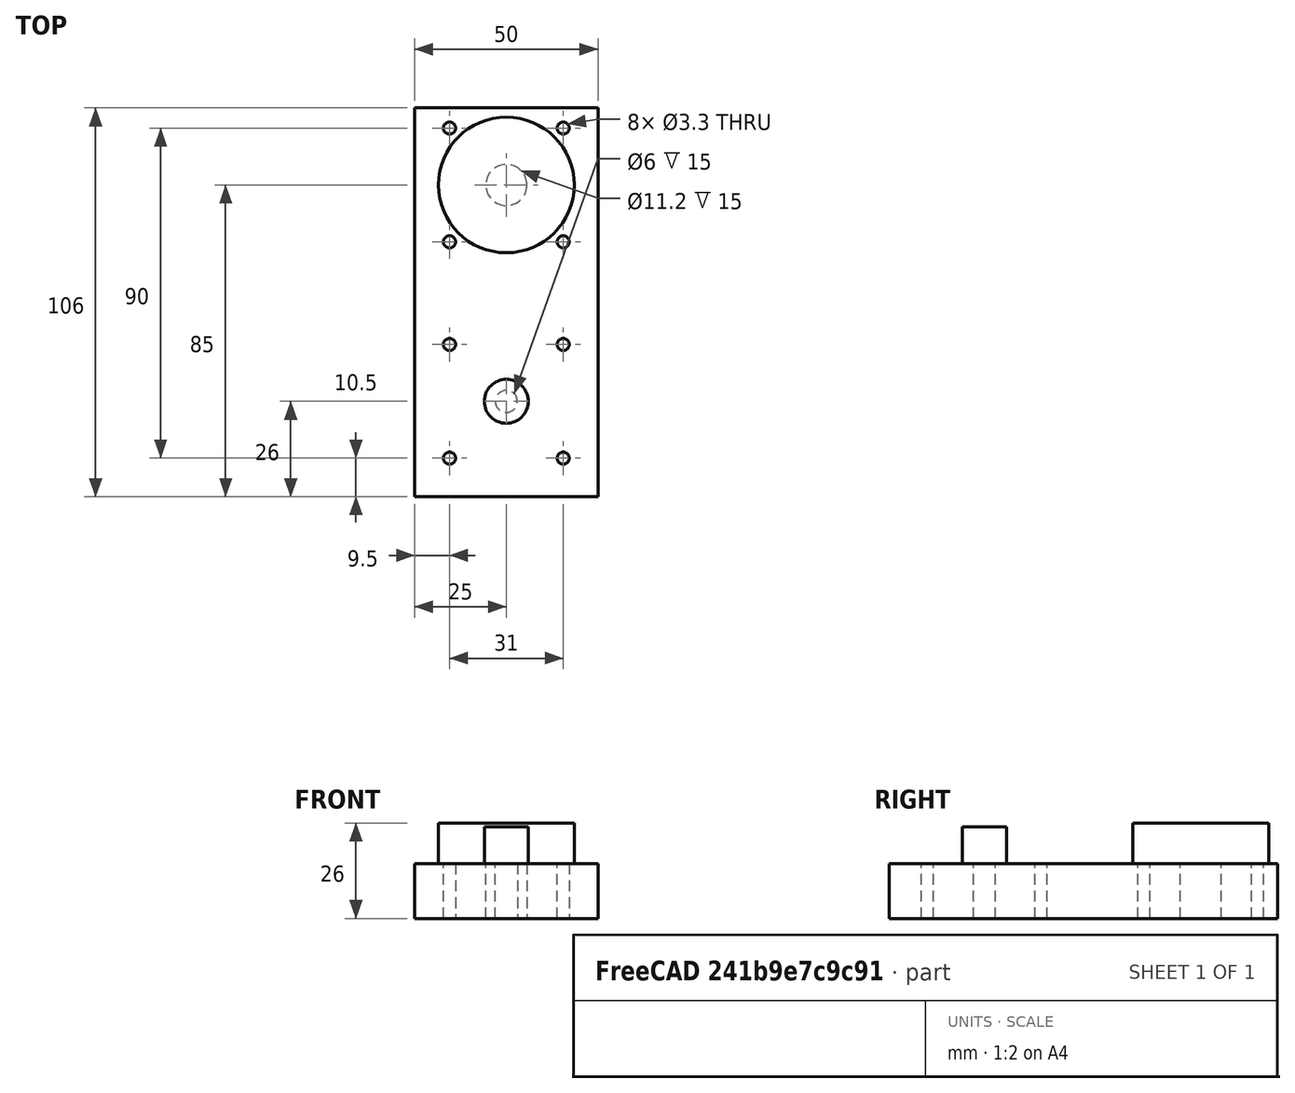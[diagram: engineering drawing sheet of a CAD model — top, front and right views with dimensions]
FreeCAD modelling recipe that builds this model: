
FCSTD DOCUMENT  (FreeCAD 0.19R)
Label: ConsBelt
License: All rights reserved
LicenseURL: http://en.wikipedia.org/wiki/All_rights_reserved
objects: Sketcher::SketchObject×5, PartDesign::Pad×3, PartDesign::Pocket×2, PartDesign::Body×1, Mesh::Feature×1
note: 16 computed .brp shape members not serialized (recipe doc carries the construction recipe); baked Part::Feature solids carry a one-line shape summary decoded from their .brp

FEATURE [Sketcher::SketchObject] Sketch
  FullyConstrained = true
  MapMode = 5
  Support = -> [XY_Plane]
  sketch-geometry (9):
    g0: Circle CenterX=0 CenterY=0 CenterZ=0 NormalX=0 NormalY=0 NormalZ=1 AngleXU=0 Radius=11.5
    g1: LineSegment StartX=-20 StartY=20 StartZ=0 EndX=20 EndY=20 EndZ=0
    g2: LineSegment StartX=20 StartY=20 StartZ=0 EndX=20 EndY=-20 EndZ=0
    g3: LineSegment StartX=20 StartY=-20 StartZ=0 EndX=-20 EndY=-20 EndZ=0
    g4: LineSegment StartX=-20 StartY=-20 StartZ=0 EndX=-20 EndY=20 EndZ=0
    g5: LineSegment StartX=-25 StartY=21 StartZ=0 EndX=25 EndY=21 EndZ=0
    g6: LineSegment StartX=25 StartY=21 StartZ=0 EndX=25 EndY=-85 EndZ=0
    g7: LineSegment StartX=25 StartY=-85 StartZ=0 EndX=-25 EndY=-85 EndZ=0
    g8: LineSegment StartX=-25 StartY=-85 StartZ=0 EndX=-25 EndY=21 EndZ=0
  constraints (24):
    c: Coincident(g0,g-1)
    c: Coincident(g1,g2)
    c: Coincident(g2,g3)
    c: Coincident(g3,g4)
    c: Coincident(g4,g1)
    c: Horizontal(g1)
    c: Horizontal(g3)
    c: Vertical(g2)
    c: Vertical(g4)
    c: Equal(g2,g3)
    c: Distance(g2) = 40
    c: Symmetric(g1,g3,g0)
    c: Diameter(g0) = 23
    c: Coincident(g5,g6)
    c: Coincident(g6,g7)
    c: Coincident(g7,g8)
    c: Coincident(g8,g5)
    c: Horizontal(g7)
    c: Vertical(g6)
    c: Vertical(g8)
    c: Distance(g5) = 50
    c: Symmetric(g5,g5,g-2)
    c: DistanceY(g5) = 21
    c: DistanceY(g6) = -85
FEATURE [PartDesign::Pad] Pad
  Direction = (1,1,1)
  Length = 15
  Length2 = 100
  Profile = -> Sketch
  Type = 0
FEATURE [Sketcher::SketchObject] Sketch001
  FullyConstrained = true
  MapMode = 5
  Placement = pos=(0,0,15) rot=(0,0,1;0rad)
  Support = -> [Pad]
  sketch-geometry (5):
    g0: Circle CenterX=0 CenterY=0 CenterZ=0 NormalX=0 NormalY=0 NormalZ=1 AngleXU=0 Radius=5.6
    g1: Circle CenterX=-15.5 CenterY=15.5 CenterZ=0 NormalX=0 NormalY=0 NormalZ=1 AngleXU=0 Radius=1.65
    g2: Circle CenterX=15.5 CenterY=15.5 CenterZ=0 NormalX=0 NormalY=0 NormalZ=1 AngleXU=0 Radius=1.65
    g3: Circle CenterX=-15.5 CenterY=-15.5 CenterZ=0 NormalX=0 NormalY=0 NormalZ=1 AngleXU=0 Radius=1.65
    g4: Circle CenterX=15.5 CenterY=-15.5 CenterZ=0 NormalX=0 NormalY=0 NormalZ=1 AngleXU=0 Radius=1.65
  constraints (11):
    c: Coincident(g0,g-1)
    c: Diameter(g0) = 11.2
    c: Diameter(g4) = 3.3
    c: Equal(g4,g2)
    c: Equal(g4,g1)
    c: Equal(g4,g3)
    c: Symmetric(g2,g3,g0)
    c: Symmetric(g4,g1,g0)
    c: Symmetric(g2,g1,g-2)
    c: Distance(g2,g1) = 31
    c: Distance(g4,g2) = 31
FEATURE [PartDesign::Pocket] Pocket
  BaseFeature = -> Pad
  Length = 5
  Length2 = 100
  Profile = -> Sketch001
  Type = 1
FEATURE [Sketcher::SketchObject] Sketch002
  FullyConstrained = true
  MapMode = 5
  Placement = pos=(0,0,15) rot=(0,0,1;0rad)
  Support = -> [Pocket]
  sketch-geometry (2):
    g0: Circle CenterX=0 CenterY=0 CenterZ=0 NormalX=0 NormalY=0 NormalZ=1 AngleXU=0 Radius=22
    g1: Circle CenterX=0 CenterY=0 CenterZ=0 NormalX=0 NormalY=0 NormalZ=1 AngleXU=0 Radius=18.5
  constraints (4):
    c: Coincident(g1,g0)
    c: Diameter(g1) = 37
    c: Diameter(g0) = 44
    c: Coincident(g0,g-1)
FEATURE [PartDesign::Pad] Pad001
  BaseFeature = -> Pocket
  Direction = (1,1,1)
  Length = 11
  Length2 = 100
  Profile = -> Sketch002
  Type = 0
FEATURE [Sketcher::SketchObject] Sketch003
  ExternalGeometry = -> [Pad001]
  FullyConstrained = false
  MapMode = 5
  Placement = pos=(0,0,15) rot=(0,0,1;0rad)
  Support = -> [Pad001]
  sketch-geometry (11):
    g0: Circle CenterX=0 CenterY=-59 CenterZ=0 NormalX=0 NormalY=0 NormalZ=1 AngleXU=0 Radius=6
    g1: Circle CenterX=0 CenterY=-59 CenterZ=0 NormalX=0 NormalY=0 NormalZ=1 AngleXU=0 Radius=7.5
    g2: Circle CenterX=-15.5 CenterY=-43.5 CenterZ=0 NormalX=0 NormalY=0 NormalZ=1 AngleXU=0 Radius=1.65
    g3: Circle CenterX=15.5 CenterY=-43.5 CenterZ=0 NormalX=0 NormalY=0 NormalZ=1 AngleXU=0 Radius=1.65
    g4: Circle CenterX=-15.5 CenterY=-74.5 CenterZ=0 NormalX=0 NormalY=0 NormalZ=1 AngleXU=0 Radius=1.65
    g5: Circle CenterX=15.5 CenterY=-74.5 CenterZ=0 NormalX=0 NormalY=0 NormalZ=1 AngleXU=0 Radius=1.65
    g6: Circle CenterX=0 CenterY=-59 CenterZ=0 NormalX=0 NormalY=0 NormalZ=1 AngleXU=0 Radius=3
    g7: LineSegment StartX=-17.4797 StartY=-6.15492 StartZ=0 EndX=-5.86638 EndY=-60.2592 EndZ=0
    g8: Circle CenterX=11.7737 CenterY=-32.5924 CenterZ=0 NormalX=0 NormalY=0 NormalZ=1 AngleXU=0 Radius=6
    g9: LineSegment StartX=5.9999 StartY=-58.9647 StartZ=0 EndX=5.83971 EndY=-31.7049 EndZ=0
    g10: LineSegment StartX=18.1552 StartY=-3.55508 StartZ=0 EndX=6.65018 EndY=-29.47 EndZ=0
  constraints (23):
    c: PointOnObject(g0,g-2)
    c: Diameter(g1) = 15
    c: Diameter(g0) = 12
    c: Diameter(g3) = 3.3
    c: Equal(g3,g2)
    c: Equal(g3,g4)
    c: Equal(g3,g5)
    c: Symmetric(g3,g2,g-2)
    c: Distance(g3,g2) = 31
    c: Distance(g5,g3) = 31
    c: Symmetric(g5,g4,g-2)
    c: Symmetric(g3,g4,g0)
    c: Diameter(g6) = 6
    c: Coincident(g6,g0)
    c: PointOnObject(g7,g0)
    c: Tangent(g7,g0)
    c: Diameter(g8) = 12
    c: PointOnObject(g9,g0)
    c: PointOnObject(g9,g8)
    c: Tangent(g9,g0)
    c: PointOnObject(g10,g8)
    c: Coincident(g1,g6)
    c: Distance(g-1,g6) = 59
FEATURE [PartDesign::Pocket] Pocket001
  BaseFeature = -> Pad001
  Length = 5
  Length2 = 100
  Profile = -> Sketch003
  Type = 1
FEATURE [Sketcher::SketchObject] Sketch004
  ExternalGeometry = -> [Pocket001]
  FullyConstrained = false
  MapMode = 5
  Placement = pos=(0,0,15) rot=(0,0,1;0rad)
  Support = -> [Pocket001]
  sketch-geometry (1):
    g0: Circle CenterX=0 CenterY=-59 CenterZ=0 NormalX=0 NormalY=0 NormalZ=1 AngleXU=0 Radius=6
  constraints (2):
    c: PointOnObject(g0,g-2)
    c: Distance(g-1,g0) = 59
FEATURE [PartDesign::Pad] Pad002
  BaseFeature = -> Pocket001
  Direction = (1,1,1)
  Length = 10
  Length2 = 100
  Profile = -> Sketch004
  Type = 0
FEATURE [PartDesign::Body] Body
  Group = -> [Sketch,Pad,Sketch001,Pocket,Sketch002,Pad001,Sketch003,Pocket001,Sketch004,Pad002]
  Origin = -> Origin
  Tip = -> Pad002
FEATURE [Mesh::Feature] Mesh  label="Pad002 (Meshed)"
